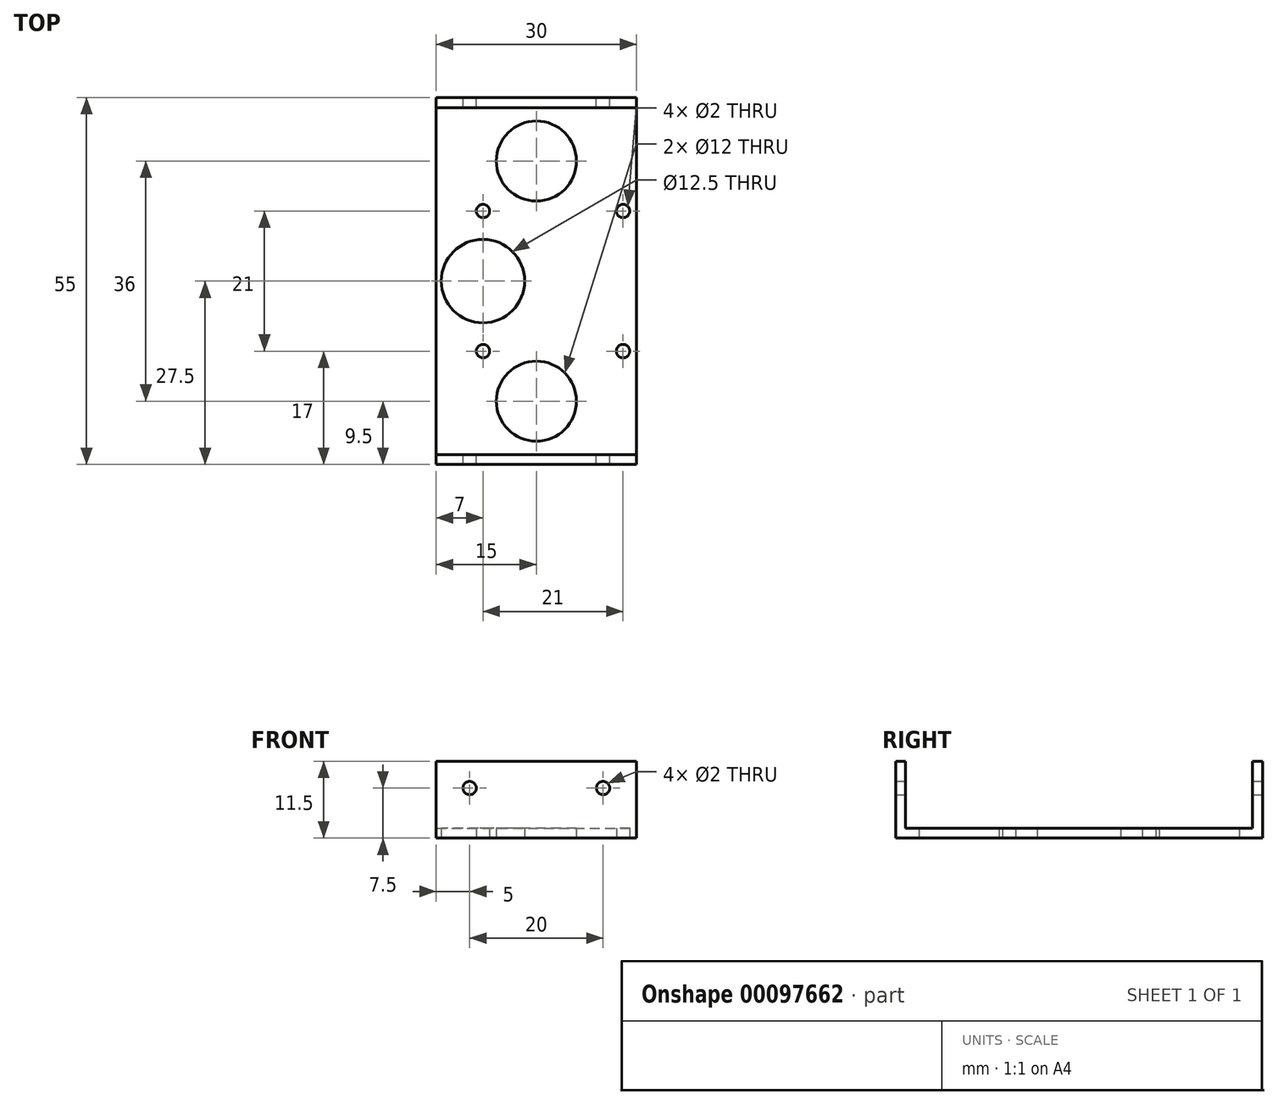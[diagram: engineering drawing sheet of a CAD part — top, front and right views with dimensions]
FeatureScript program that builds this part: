
annotation { "Feature Type Name" : "Feature", "Feature Type Description" : "" }
export const myFeature = defineFeature(function(context is Context, id is Id, definition is map)
    precondition{}
    {
        {
            var Q0;
            Q0=qCreatedBy(makeId("Top.planeOp"),FACE);
            var sketch = newSketch(context, id + "F0", { "sketchPlane" : qUnion([Q0])});
            skLineSegment(sketch, "E0.bottom", {"start": v(-15, -20) * mm, "end": v(15, -20) * mm});
            skLineSegment(sketch, "E0.top", {"start": v(-15, 35) * mm, "end": v(15, 35) * mm});
            skLineSegment(sketch, "E0.left", {"start": v(-15, -20) * mm, "end": v(-15, 35) * mm});
            skLineSegment(sketch, "E0.right", {"start": v(15, -20) * mm, "end": v(15, 35) * mm});
            skPoint(sketch, "E1", {"position": v(0, 35) * mm});
            skLineSegment(sketch, "E2", {"start": v(-15, 7.5) * mm, "end": v(15, 7.5) * mm, "construction": true});
            skCircle(sketch, "E3", {"center": v(-8, 7.5) * mm, "radius": 6.25 * mm});
            skCircle(sketch, "E4", {"center": v(-8, -3) * mm, "radius": 1 * mm});
            skCircle(sketch, "E5", {"center": v(13, -3) * mm, "radius": 1 * mm});
            skCircle(sketch, "E6.MirrorC", {"center": v(-8, 18) * mm, "radius": 1 * mm});
            skCircle(sketch, "E7.MirrorC", {"center": v(13, 18) * mm, "radius": 1 * mm});
            skCircle(sketch, "E8", {"center": v(0, 25.5) * mm, "radius": 6 * mm});
            skCircle(sketch, "E9.MirrorC", {"center": v(0, -10.5) * mm, "radius": 6 * mm});
            skSolve(sketch);
        }
        {
            var Q0;
            Q0=qSketchRegion(id+"F0",true);
            extrude(context, id + "F1", {"entities" : qUnion([Q0]), "depth" : 1.5 * mm});
        }
        {
            var Q0;
            Q0=makeQuery(id+"F1.opExtrude","CAP_FACE",FACE,{"disambiguationData":[OSD([sQuery(id+"F0.wireOp",EDGE,"E0.bottom"),sQuery(id+"F0.wireOp",EDGE,"E0.top"),sQuery(id+"F0.wireOp",EDGE,"E0.left"),sQuery(id+"F0.wireOp",EDGE,"E0.right"),sQuery(id+"F0.wireOp",EDGE,"E3"),sQuery(id+"F0.wireOp",EDGE,"E4"),sQuery(id+"F0.wireOp",EDGE,"E5"),sQuery(id+"F0.wireOp",EDGE,"E6.MirrorC"),sQuery(id+"F0.wireOp",EDGE,"E7.MirrorC")])],"isStart":false});
            var sketch = newSketch(context, id + "F2", { "sketchPlane" : qUnion([Q0])});
            skLineSegment(sketch, "E10.bottom", {"start": v(-15, 35) * mm, "end": v(15, 35) * mm});
            skLineSegment(sketch, "E10.top", {"start": v(-15, 33.5) * mm, "end": v(15, 33.5) * mm});
            skLineSegment(sketch, "E10.left", {"start": v(-15, 35) * mm, "end": v(-15, 33.5) * mm});
            skLineSegment(sketch, "E10.right", {"start": v(15, 35) * mm, "end": v(15, 33.5) * mm});
            skLineSegment(sketch, "E11.bottom", {"start": v(-15, -20) * mm, "end": v(15, -20) * mm});
            skLineSegment(sketch, "E11.top", {"start": v(-15, -18.5) * mm, "end": v(15, -18.5) * mm});
            skLineSegment(sketch, "E11.left", {"start": v(-15, -20) * mm, "end": v(-15, -18.5) * mm});
            skLineSegment(sketch, "E11.right", {"start": v(15, -20) * mm, "end": v(15, -18.5) * mm});
            skSolve(sketch);
        }
        {
            var Q0;
            Q0=qSketchRegion(id+"F2",true);
            extrude(context, id + "F3", {"entities" : qUnion([Q0]), "operationType" : NewBodyOperationType.ADD, "depth" : 10 * mm});
        }
        {
            var Q0;
            Q0=makeQuery(id+"F3.boolean.opBoolean","MERGE",FACE,{"derivedFrom":[makeQuery(id+"F1.opExtrude","SWEPT_FACE",FACE,{"disambiguationData":[OSD([sQuery(id+"F0.wireOp",EDGE,"E0.top")])]}),makeQuery(id+"F3.opExtrude","SWEPT_FACE",FACE,{"disambiguationData":[OSD([sQuery(id+"F2.wireOp",EDGE,"E10.bottom")])]})]});
            var sketch = newSketch(context, id + "F4", { "sketchPlane" : qUnion([Q0])});
            skCircle(sketch, "E12", {"center": v(-10, 7.5) * mm, "radius": 1 * mm});
            skCircle(sketch, "E13.MirrorC", {"center": v(10, 7.5) * mm, "radius": 1 * mm});
            skSolve(sketch);
        }
        {
            var Q0;
            Q0=qSketchRegion(id+"F4",true);
            extrude(context, id + "F5", {"entities" : qUnion([Q0]), "operationType" : NewBodyOperationType.REMOVE, "endBound" : BoundingType.THROUGH_ALL, "oppositeDirection" : true, "depth" : 25 * mm});
        }
    });
